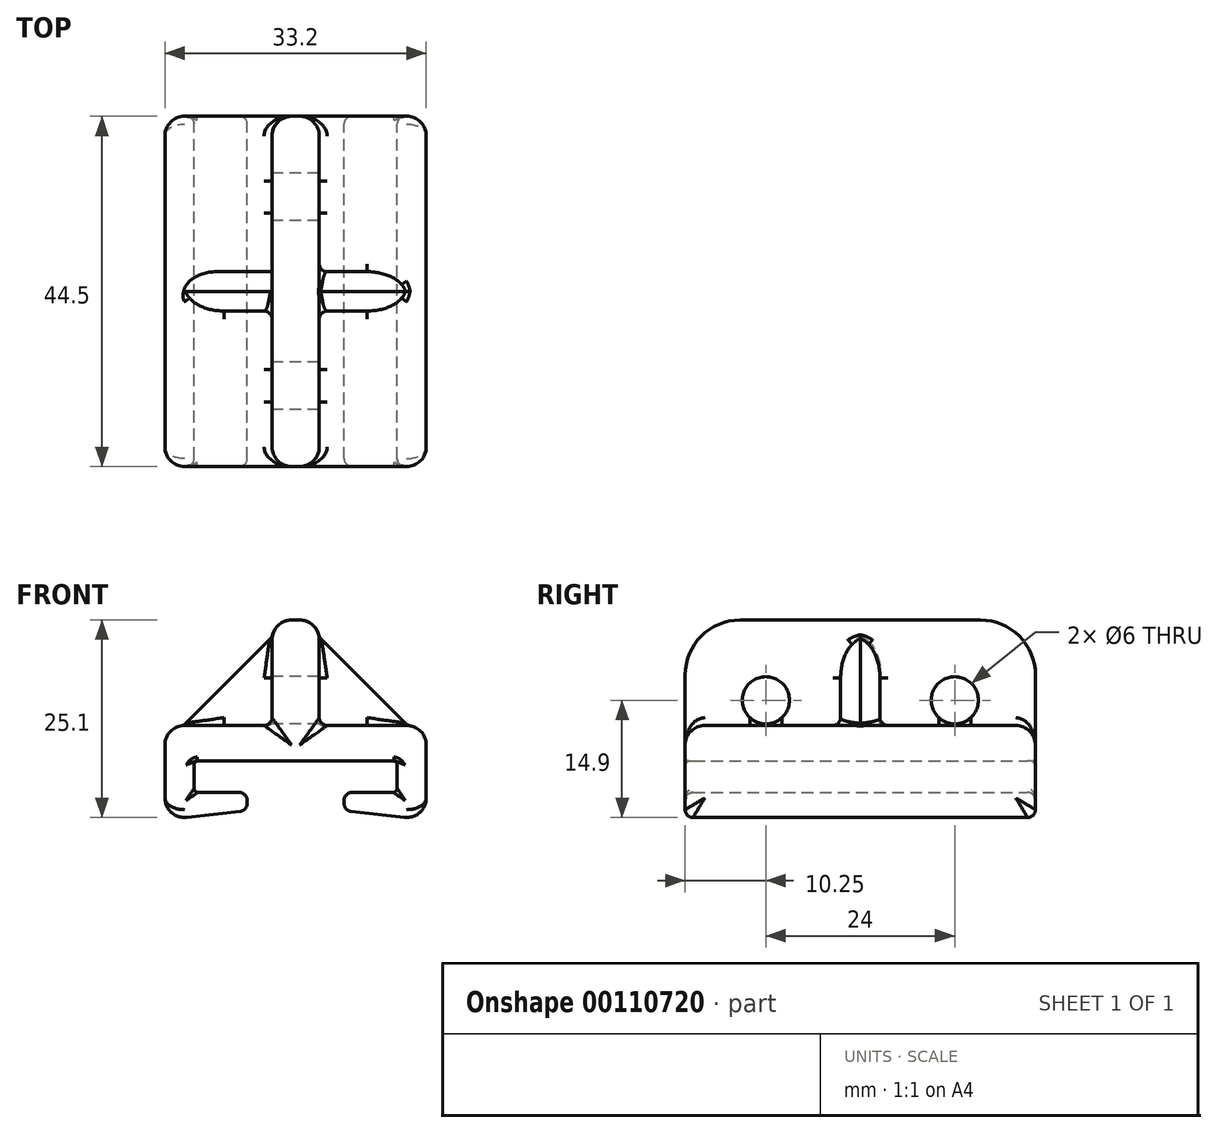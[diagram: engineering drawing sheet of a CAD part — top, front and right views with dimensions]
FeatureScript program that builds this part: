
annotation { "Feature Type Name" : "Feature", "Feature Type Description" : "" }
export const myFeature = defineFeature(function(context is Context, id is Id, definition is map)
    precondition{}
    {
        {
            var Q0;
            Q0=qCreatedBy(makeId("Front.planeOp"),FACE);
            var sketch = newSketch(context, id + "F0", { "sketchPlane" : qUnion([Q0])});
            skLineSegment(sketch, "E0", {"start": v(0, 0) * mm, "end": v(-12.9, 0) * mm});
            skLineSegment(sketch, "E1", {"start": v(-12.9, 0) * mm, "end": v(-12.9, -4) * mm});
            skLineSegment(sketch, "E2", {"start": v(-12.9, -4) * mm, "end": v(-6.15, -4) * mm});
            skLineSegment(sketch, "E3", {"start": v(-6.15, -4) * mm, "end": v(-6.15, -6.3) * mm});
            skLineSegment(sketch, "E4", {"start": v(-6.15, -6.3) * mm, "end": v(-16.6, -7.5) * mm});
            skLineSegment(sketch, "E5", {"start": v(-16.6, -7.5) * mm, "end": v(-16.6, 4.5) * mm});
            skLineSegment(sketch, "E6", {"start": v(-16.6, 4.5) * mm, "end": v(-3, 4.5) * mm});
            skLineSegment(sketch, "E7", {"start": v(-3, 4.5) * mm, "end": v(-3, 17.9) * mm});
            skLineSegment(sketch, "E8", {"start": v(-3, 17.9) * mm, "end": v(0, 17.9) * mm});
            skLineSegment(sketch, "E9.MirrorCS", {"start": v(6.15, -4) * mm, "end": v(6.15, -6.3) * mm});
            skLineSegment(sketch, "E10.MirrorCS", {"start": v(3, 17.9) * mm, "end": v(0, 17.9) * mm});
            skLineSegment(sketch, "E11.MirrorCS", {"start": v(12.9, -4) * mm, "end": v(6.15, -4) * mm});
            skLineSegment(sketch, "E12.MirrorCS", {"start": v(3, 4.5) * mm, "end": v(3, 17.9) * mm});
            skLineSegment(sketch, "E13.MirrorCS", {"start": v(16.6, 4.5) * mm, "end": v(3, 4.5) * mm});
            skLineSegment(sketch, "E14.MirrorCS", {"start": v(16.6, -7.5) * mm, "end": v(16.6, 4.5) * mm});
            skLineSegment(sketch, "E15.MirrorCS", {"start": v(6.15, -6.3) * mm, "end": v(16.6, -7.5) * mm});
            skLineSegment(sketch, "E16.MirrorCS", {"start": v(0, 0) * mm, "end": v(12.9, 0) * mm});
            skLineSegment(sketch, "E17.MirrorCS", {"start": v(12.9, 0) * mm, "end": v(12.9, -4) * mm});
            skSolve(sketch);
        }
        {
            var Q0;
            Q0 = qSketchRegion(id + "F0", true);
            extrude(context, id + "F1", {"entities" : qUnion([Q0]), "depth" : 44.5 * mm, "symmetric" : true});
        }
        {
            var Q0;
            Q0=qCreatedBy(makeId("Front.planeOp"),FACE);
            var sketch = newSketch(context, id + "F2", { "sketchPlane" : qUnion([Q0])});
            skLineSegment(sketch, "E18.0", {"start": v(-3, 4.5) * mm, "end": v(-3, 15.8) * mm});
            skLineSegment(sketch, "E19.0", {"start": v(-14.3, 4.5) * mm, "end": v(-3, 4.5) * mm});
            skLineSegment(sketch, "E20", {"start": v(-14.3, 4.5) * mm, "end": v(-3, 15.8) * mm});
            skPoint(sketch, "E21.orphan", {"position": v(-3, 17.9) * mm});
            skPoint(sketch, "E22.orphan", {"position": v(-16.6, 4.5) * mm});
            skPoint(sketch, "E23.MirrorP", {"position": v(3, 17.9) * mm});
            skPoint(sketch, "E24.MirrorP", {"position": v(16.6, 4.5) * mm});
            skLineSegment(sketch, "E25.MirrorCS", {"start": v(3, 4.5) * mm, "end": v(3, 15.8) * mm});
            skLineSegment(sketch, "E26.MirrorCS", {"start": v(14.3, 4.5) * mm, "end": v(3, 15.8) * mm});
            skLineSegment(sketch, "E27.MirrorCS", {"start": v(14.3, 4.5) * mm, "end": v(3, 4.5) * mm});
            skSolve(sketch);
        }
        {
            var Q0;
            Q0 = qSketchRegion(id + "F2", true);
            extrude(context, id + "F3", {"entities" : qUnion([Q0]), "operationType" : NewBodyOperationType.ADD, "depth" : 5 * mm, "symmetric" : true});
        }
        {
            var Q0;
            Q0=makeQuery(id+"F1.opExtrude","CAP_EDGE",EDGE,{"disambiguationData":[OSD([sQuery(id+"F0.wireOp",EDGE,"E8"),sQuery(id+"F0.wireOp",EDGE,"E10.MirrorCS")])],"isStart":false});
            var Q1;
            Q1=makeQuery(id+"F1.opExtrude","CAP_EDGE",EDGE,{"disambiguationData":[OSD([sQuery(id+"F0.wireOp",EDGE,"E8"),sQuery(id+"F0.wireOp",EDGE,"E10.MirrorCS")])],"isStart":true});
            fillet(context, id + "F4", {"entities" : qUnion([Q0, Q1]), "radius" : 7 * mm, "tangentPropagation" : true, "allowEdgeOverflow" : false});
        }
        {
            var Q0;
            Q0=makeQuery(id+"F1.opExtrude","SWEPT_FACE",FACE,{"disambiguationData":[OSD([sQuery(id+"F0.wireOp",EDGE,"E12.MirrorCS")])]});
            var sketch = newSketch(context, id + "F5", { "sketchPlane" : qUnion([Q0])});
            skPoint(sketch, "E28", {"position": v(-12, 7.7) * mm});
            skPoint(sketch, "E29", {"position": v(12, 7.7) * mm});
            skSolve(sketch);
        }
        {
            var Q0;
            Q0=sQuery(id+"F5.wireOp",VERTEX,"E28");
            var Q1;
            Q1=sQuery(id+"F5.wireOp",VERTEX,"E29");
            var Q2;
            Q2=makeQuery(id+"F1.opExtrude","SWEPT_BODY",BODY,{"disambiguationData":[OSD([sQuery(id+"F0.wireOp",EDGE,"E0"),sQuery(id+"F0.wireOp",EDGE,"E1"),sQuery(id+"F0.wireOp",EDGE,"E2"),sQuery(id+"F0.wireOp",EDGE,"E3"),sQuery(id+"F0.wireOp",EDGE,"E4"),sQuery(id+"F0.wireOp",EDGE,"E5"),sQuery(id+"F0.wireOp",EDGE,"E6"),sQuery(id+"F0.wireOp",EDGE,"E7"),sQuery(id+"F0.wireOp",EDGE,"E8"),sQuery(id+"F0.wireOp",EDGE,"E9.MirrorCS"),sQuery(id+"F0.wireOp",EDGE,"E10.MirrorCS"),sQuery(id+"F0.wireOp",EDGE,"E11.MirrorCS"),sQuery(id+"F0.wireOp",EDGE,"E12.MirrorCS"),sQuery(id+"F0.wireOp",EDGE,"E13.MirrorCS"),sQuery(id+"F0.wireOp",EDGE,"E14.MirrorCS"),sQuery(id+"F0.wireOp",EDGE,"E15.MirrorCS"),sQuery(id+"F0.wireOp",EDGE,"E16.MirrorCS"),sQuery(id+"F0.wireOp",EDGE,"E17.MirrorCS")])]});
            hole(context, id + "F6", {"style" : HoleStyle.SIMPLE, "endStyle" : HoleEndStyle.THROUGH, "holeDiameter" : 6 * mm, "locations" : qUnion([Q0, Q1]), "scope" : qUnion([Q2]), "isTappedThrough" : true, "startStyle" : HoleStartStyle.PART});
        }
        {
            var Q0;
            Q0=makeQuery(id+"F3.opExtrude","CAP_EDGE",EDGE,{"disambiguationData":[OSD([sQuery(id+"F2.wireOp",EDGE,"E26.MirrorCS")])],"isStart":false});
            var Q1;
            Q1=makeQuery(id+"F3.opExtrude","CAP_EDGE",EDGE,{"disambiguationData":[OSD([sQuery(id+"F2.wireOp",EDGE,"E26.MirrorCS")])],"isStart":true});
            var Q2;
            Q2=makeQuery(id+"F3.opExtrude","CAP_EDGE",EDGE,{"disambiguationData":[OSD([sQuery(id+"F2.wireOp",EDGE,"E20")])],"isStart":true});
            var Q3;
            Q3=makeQuery(id+"F3.opExtrude","CAP_EDGE",EDGE,{"disambiguationData":[OSD([sQuery(id+"F2.wireOp",EDGE,"E20")])],"isStart":false});
            fillet(context, id + "F7", {"entities" : qUnion([Q0, Q1, Q2, Q3]), "radius" : 3 * mm, "tangentPropagation" : true, "allowEdgeOverflow" : false});
        }
        {
            var Q0;
            Q0=makeQuery(id+"F1.opExtrude","SWEPT_EDGE",EDGE,{"disambiguationData":[OSD([sQuery(id+"F0.wireOp",EDGE,"E9.MirrorCS"),sQuery(id+"F0.wireOp",EDGE,"E15.MirrorCS")])]});
            var Q1;
            Q1=makeQuery(id+"F1.opExtrude","SWEPT_EDGE",EDGE,{"disambiguationData":[OSD([sQuery(id+"F0.wireOp",EDGE,"E9.MirrorCS"),sQuery(id+"F0.wireOp",EDGE,"E11.MirrorCS")])]});
            var Q2;
            Q2=makeQuery(id+"F1.opExtrude","SWEPT_EDGE",EDGE,{"disambiguationData":[OSD([sQuery(id+"F0.wireOp",EDGE,"E2"),sQuery(id+"F0.wireOp",EDGE,"E3")])]});
            var Q3;
            Q3=makeQuery(id+"F1.opExtrude","SWEPT_EDGE",EDGE,{"disambiguationData":[OSD([sQuery(id+"F0.wireOp",EDGE,"E3"),sQuery(id+"F0.wireOp",EDGE,"E4")])]});
            fillet(context, id + "F8", {"entities" : qUnion([Q0, Q1, Q2, Q3]), "radius" : 1 * mm, "tangentPropagation" : true, "allowEdgeOverflow" : false});
        }
        {
            var Q0;
            Q0=makeQuery(id+"F1.opExtrude","SWEPT_FACE",FACE,{"disambiguationData":[OSD([sQuery(id+"F0.wireOp",EDGE,"E14.MirrorCS")])]});
            var Q1;
            Q1=makeQuery(id+"F1.opExtrude","SWEPT_FACE",FACE,{"disambiguationData":[OSD([sQuery(id+"F0.wireOp",EDGE,"E5")])]});
            var Q2;
            Q2=makeQuery(id+"F1.opExtrude","SWEPT_EDGE",EDGE,{"disambiguationData":[OSD([sQuery(id+"F0.wireOp",EDGE,"E7"),sQuery(id+"F0.wireOp",EDGE,"E8")])]});
            var Q3;
            Q3=makeQuery(id+"F1.opExtrude","SWEPT_EDGE",EDGE,{"disambiguationData":[OSD([sQuery(id+"F0.wireOp",EDGE,"E10.MirrorCS"),sQuery(id+"F0.wireOp",EDGE,"E12.MirrorCS")])]});
            var Q4;
            Q4=makeQuery(id+"F1.opExtrude","CAP_EDGE",EDGE,{"disambiguationData":[OSD([sQuery(id+"F0.wireOp",EDGE,"E13.MirrorCS")])],"isStart":true});
            var Q5;
            Q5=makeQuery(id+"F1.opExtrude","CAP_EDGE",EDGE,{"disambiguationData":[OSD([sQuery(id+"F0.wireOp",EDGE,"E6")])],"isStart":true});
            var Q6;
            Q6=makeQuery(id+"F1.opExtrude","CAP_EDGE",EDGE,{"disambiguationData":[OSD([sQuery(id+"F0.wireOp",EDGE,"E13.MirrorCS")])],"isStart":false});
            var Q7;
            Q7=makeQuery(id+"F1.opExtrude","CAP_EDGE",EDGE,{"disambiguationData":[OSD([sQuery(id+"F0.wireOp",EDGE,"E6")])],"isStart":false});
            fillet(context, id + "F9", {"entities" : qUnion([Q0, Q1, Q2, Q3, Q4, Q5, Q6, Q7]), "radius" : 2.5 * mm, "tangentPropagation" : true, "allowEdgeOverflow" : false});
        }
        {
            var Q0;
            Q0=makeQuery(id+"F3.opExtrude","CAP_EDGE",EDGE,{"disambiguationData":[OSD([sQuery(id+"F2.wireOp",EDGE,"E19.0")])],"isStart":true});
            var Q1;
            Q1=makeQuery(id+"F3.opExtrude","CAP_EDGE",EDGE,{"disambiguationData":[OSD([sQuery(id+"F2.wireOp",EDGE,"E18.0")])],"isStart":true});
            var Q2;
            Q2=makeQuery(id+"F3.opExtrude","CAP_FACE",FACE,{"disambiguationData":[OSD([sQuery(id+"F2.wireOp",EDGE,"E25.MirrorCS"),sQuery(id+"F2.wireOp",EDGE,"E26.MirrorCS"),sQuery(id+"F2.wireOp",EDGE,"E27.MirrorCS")])],"isStart":true});
            var Q3;
            Q3=makeQuery(id+"F3.opExtrude","CAP_FACE",FACE,{"disambiguationData":[OSD([sQuery(id+"F2.wireOp",EDGE,"E25.MirrorCS"),sQuery(id+"F2.wireOp",EDGE,"E26.MirrorCS"),sQuery(id+"F2.wireOp",EDGE,"E27.MirrorCS")])],"isStart":false});
            var Q4;
            Q4=makeQuery(id+"F3.opExtrude","CAP_FACE",FACE,{"disambiguationData":[OSD([sQuery(id+"F2.wireOp",EDGE,"E18.0"),sQuery(id+"F2.wireOp",EDGE,"E19.0"),sQuery(id+"F2.wireOp",EDGE,"E20")])],"isStart":false});
            var Q5;
            Q5=makeQuery(id+"F1.opExtrude","CAP_EDGE",EDGE,{"disambiguationData":[OSD([sQuery(id+"F0.wireOp",EDGE,"E4")])],"isStart":false});
            var Q6;
            Q6=makeQuery(id+"F1.opExtrude","CAP_EDGE",EDGE,{"disambiguationData":[OSD([sQuery(id+"F0.wireOp",EDGE,"E15.MirrorCS")])],"isStart":false});
            var Q7;
            Q7=makeQuery(id+"F1.opExtrude","CAP_EDGE",EDGE,{"disambiguationData":[OSD([sQuery(id+"F0.wireOp",EDGE,"E17.MirrorCS")])],"isStart":false});
            var Q8;
            Q8=makeQuery(id+"F1.opExtrude","CAP_EDGE",EDGE,{"disambiguationData":[OSD([sQuery(id+"F0.wireOp",EDGE,"E1")])],"isStart":false});
            var Q9;
            Q9=makeQuery(id+"F1.opExtrude","CAP_EDGE",EDGE,{"disambiguationData":[OSD([sQuery(id+"F0.wireOp",EDGE,"E2")])],"isStart":true});
            var Q10;
            Q10=makeQuery(id+"F1.opExtrude","CAP_EDGE",EDGE,{"disambiguationData":[OSD([sQuery(id+"F0.wireOp",EDGE,"E1")])],"isStart":true});
            var Q11;
            Q11=makeQuery(id+"F1.opExtrude","CAP_EDGE",EDGE,{"disambiguationData":[OSD([sQuery(id+"F0.wireOp",EDGE,"E11.MirrorCS")])],"isStart":true});
            var Q12;
            Q12=makeQuery(id+"F1.opExtrude","CAP_EDGE",EDGE,{"disambiguationData":[OSD([sQuery(id+"F0.wireOp",EDGE,"E17.MirrorCS")])],"isStart":true});
            fillet(context, id + "F10", {"entities" : qUnion([Q0, Q1, Q2, Q3, Q4, Q5, Q6, Q7, Q8, Q9, Q10, Q11, Q12]), "radius" : 1 * mm, "tangentPropagation" : true, "allowEdgeOverflow" : false});
        }
        {
            var Q0;
            Q0=makeQuery(id+"F1.opExtrude","SWEPT_EDGE",EDGE,{"disambiguationData":[OSD([sQuery(id+"F0.wireOp",EDGE,"E11.MirrorCS"),sQuery(id+"F0.wireOp",EDGE,"E17.MirrorCS")])]});
            var Q1;
            Q1=makeQuery(id+"F1.opExtrude","SWEPT_EDGE",EDGE,{"disambiguationData":[OSD([sQuery(id+"F0.wireOp",EDGE,"E1"),sQuery(id+"F0.wireOp",EDGE,"E2")])]});
            var Q2;
            Q2=makeQuery(id+"F1.opExtrude","SWEPT_FACE",FACE,{"disambiguationData":[OSD([sQuery(id+"F0.wireOp",EDGE,"E0"),sQuery(id+"F0.wireOp",EDGE,"E16.MirrorCS")])]});
            var Q3;
            Q3=makeQuery(id+"F6.hole-1.boolean.opBoolean","COPY",FACE,{"derivedFrom":makeQuery(id+"F6.hole-1.opRevolve","SWEPT_FACE",FACE,{"disambiguationData":[OSD([sQuery(id+"F6.hole-1.sketch.wireOp",EDGE,"core_line_2")])]})});
            var Q4;
            Q4=makeQuery(id+"F6.hole-0.boolean.opBoolean","COPY",FACE,{"derivedFrom":makeQuery(id+"F6.hole-0.opRevolve","SWEPT_FACE",FACE,{"disambiguationData":[OSD([sQuery(id+"F6.hole-0.sketch.wireOp",EDGE,"core_line_2")])]})});
            fillet(context, id + "F11", {"entities" : qUnion([Q0, Q1, Q2, Q3, Q4]), "radius" : .5 * mm, "tangentPropagation" : true, "allowEdgeOverflow" : false});
        }
        {
            var Q0;
            {var subQ0=sQuery(id+"F0.wireOp",EDGE,"E7");var subQ1=sQuery(id+"F0.wireOp",EDGE,"E6");Q0=makeQuery(id+"F3.boolean.opBoolean","SPLIT",EDGE,{"disambiguationData":[TD([makeQuery(id+"F3.opExtrude","CAP_FACE",FACE,{"disambiguationData":[OSD([sQuery(id+"F2.wireOp",EDGE,"E18.0"),sQuery(id+"F2.wireOp",EDGE,"E19.0"),sQuery(id+"F2.wireOp",EDGE,"E20")])],"isStart":true})])],"derivedFrom":makeQuery(id+"F1.opExtrude","SWEPT_EDGE",EDGE,{"disambiguationData":[OSD([subQ1,subQ0])]})});}
            var Q1;
            {var subQ0=sQuery(id+"F0.wireOp",EDGE,"E7");var subQ1=sQuery(id+"F0.wireOp",EDGE,"E6");Q1=makeQuery(id+"F3.boolean.opBoolean","SPLIT",EDGE,{"disambiguationData":[TD([makeQuery(id+"F3.opExtrude","CAP_FACE",FACE,{"disambiguationData":[OSD([sQuery(id+"F2.wireOp",EDGE,"E18.0"),sQuery(id+"F2.wireOp",EDGE,"E19.0"),sQuery(id+"F2.wireOp",EDGE,"E20")])],"isStart":true})])],"derivedFrom":makeQuery(id+"F1.opExtrude","SWEPT_EDGE",EDGE,{"disambiguationData":[OSD([subQ1,subQ0])]})});}
            var Q2;
            {var subQ0=sQuery(id+"F0.wireOp",EDGE,"E7");var subQ1=sQuery(id+"F0.wireOp",EDGE,"E6");Q2=makeQuery(id+"F3.boolean.opBoolean","SPLIT",EDGE,{"disambiguationData":[TD([makeQuery(id+"F3.opExtrude","CAP_FACE",FACE,{"disambiguationData":[OSD([sQuery(id+"F2.wireOp",EDGE,"E18.0"),sQuery(id+"F2.wireOp",EDGE,"E19.0"),sQuery(id+"F2.wireOp",EDGE,"E20")])],"isStart":false})])],"derivedFrom":makeQuery(id+"F1.opExtrude","SWEPT_EDGE",EDGE,{"disambiguationData":[OSD([subQ1,subQ0])]})});}
            var Q3;
            {var subQ0=sQuery(id+"F0.wireOp",EDGE,"E7");var subQ1=sQuery(id+"F0.wireOp",EDGE,"E6");Q3=makeQuery(id+"F3.boolean.opBoolean","SPLIT",EDGE,{"disambiguationData":[TD([makeQuery(id+"F3.opExtrude","CAP_FACE",FACE,{"disambiguationData":[OSD([sQuery(id+"F2.wireOp",EDGE,"E18.0"),sQuery(id+"F2.wireOp",EDGE,"E19.0"),sQuery(id+"F2.wireOp",EDGE,"E20")])],"isStart":false})])],"derivedFrom":makeQuery(id+"F1.opExtrude","SWEPT_EDGE",EDGE,{"disambiguationData":[OSD([subQ1,subQ0])]})});}
            var Q4;
            {var subQ0=sQuery(id+"F0.wireOp",EDGE,"E13.MirrorCS");var subQ1=sQuery(id+"F0.wireOp",EDGE,"E12.MirrorCS");Q4=makeQuery(id+"F3.boolean.opBoolean","SPLIT",EDGE,{"disambiguationData":[TD([makeQuery(id+"F3.opExtrude","CAP_FACE",FACE,{"disambiguationData":[OSD([sQuery(id+"F2.wireOp",EDGE,"E25.MirrorCS"),sQuery(id+"F2.wireOp",EDGE,"E26.MirrorCS"),sQuery(id+"F2.wireOp",EDGE,"E27.MirrorCS")])],"isStart":true})])],"derivedFrom":makeQuery(id+"F1.opExtrude","SWEPT_EDGE",EDGE,{"disambiguationData":[OSD([subQ1,subQ0])]})});}
            var Q5;
            {var subQ0=sQuery(id+"F0.wireOp",EDGE,"E13.MirrorCS");var subQ1=sQuery(id+"F0.wireOp",EDGE,"E12.MirrorCS");Q5=makeQuery(id+"F3.boolean.opBoolean","SPLIT",EDGE,{"disambiguationData":[TD([makeQuery(id+"F3.opExtrude","CAP_FACE",FACE,{"disambiguationData":[OSD([sQuery(id+"F2.wireOp",EDGE,"E25.MirrorCS"),sQuery(id+"F2.wireOp",EDGE,"E26.MirrorCS"),sQuery(id+"F2.wireOp",EDGE,"E27.MirrorCS")])],"isStart":true})])],"derivedFrom":makeQuery(id+"F1.opExtrude","SWEPT_EDGE",EDGE,{"disambiguationData":[OSD([subQ1,subQ0])]})});}
            var Q6;
            {var subQ0=sQuery(id+"F0.wireOp",EDGE,"E13.MirrorCS");var subQ1=sQuery(id+"F0.wireOp",EDGE,"E12.MirrorCS");Q6=makeQuery(id+"F3.boolean.opBoolean","SPLIT",EDGE,{"disambiguationData":[TD([makeQuery(id+"F3.opExtrude","CAP_FACE",FACE,{"disambiguationData":[OSD([sQuery(id+"F2.wireOp",EDGE,"E25.MirrorCS"),sQuery(id+"F2.wireOp",EDGE,"E26.MirrorCS"),sQuery(id+"F2.wireOp",EDGE,"E27.MirrorCS")])],"isStart":false})])],"derivedFrom":makeQuery(id+"F1.opExtrude","SWEPT_EDGE",EDGE,{"disambiguationData":[OSD([subQ1,subQ0])]})});}
            fillet(context, id + "F12", {"entities" : qUnion([Q0, Q1, Q2, Q3, Q4, Q5, Q6]), "radius" : 1 * mm, "tangentPropagation" : true, "allowEdgeOverflow" : false});
        }
    });
